# Revit family: BVN_BDKF
name_source: partatom
category: Mechanical Equipment
units: mm (PartAtom-declared; Revit-internal decimal feet)

## family parameters
Always vertical = Yes
Cut with Voids When Loaded = No
OmniClass Number = 23.75.00.00
OmniClass Title = Climate Control (HVAC)
Part Type = Breaks Into
Room Calculation Point = No
Round Connector Dimension = Use Diameter
Shared = No
Work Plane-Based = No

## types (13) — shared parameters
Description = Duct Fan
Frequency = 50 Hz
Manufacturer = Bahçıvan Elektrik Motor San. ve Tic. Ltd. Şti.
Material = <By Category>
Model = BDKF
Protection Class = 44
Sac = -2 mm  [stored -0.00656168 ft]
URL = http://www.bahcivanmotor.com.tr

## per-type parameters (varying)
| type | A | Air Flow | B | C | Capacitor | Corners | Current | D | E | F | G | Insulation Class | Power | Sound Pressure Level dB(A) | Speed ( d/d ) | Voltage | Weight |
| BDKF 30-15 | 150 mm | 450.0 m³/h | 300 mm | 400 mm  [stored 1.31234 ft] | 2.5 | 15 mm  [stored 0.0492126 ft] | 0 A | 320 mm  [stored 1.04987 ft] | 170 mm  [stored 0.557743 ft] | 350 mm  [stored 1.14829 ft] | 200 mm  [stored 0.656168 ft] | B | 95 W | 43 | 2450 | 230 V | 7.00 kg |
| BDKF 40-20A | 200 mm  [stored 0.656168 ft] | 1030.0 m³/h | 400 mm  [stored 1.31234 ft] | 500 mm  [stored 1.64042 ft] | 4 | 15 mm  [stored 0.0492126 ft] | 1 A | 420 mm  [stored 1.37795 ft] | 220 mm  [stored 0.721785 ft] | 450 mm  [stored 1.47638 ft] | 250 mm  [stored 0.82021 ft] | B | 135 W | 48 | 2870 | 230 V | 10.50 kg |
| BDKF 40-20B | 200 mm  [stored 0.656168 ft] | 1150.0 m³/h | 400 mm  [stored 1.31234 ft] | 500 mm  [stored 1.64042 ft] | 5 | 15 mm  [stored 0.0492126 ft] | 1 A | 420 mm  [stored 1.37795 ft] | 220 mm  [stored 0.721785 ft] | 450 mm  [stored 1.47638 ft] | 250 mm  [stored 0.82021 ft] | B | 180 W | 54 | 2650 | 230 V | 11.00 kg |
| BDKF 50-25 | 250 mm  [stored 0.82021 ft] | 1700.0 m³/h | 500 mm  [stored 1.64042 ft] | 565 mm  [stored 1.85367 ft] | 6 | 20 mm  [stored 0.0656168 ft] | 1 A | 520 mm  [stored 1.70604 ft] | 270 mm  [stored 0.885827 ft] | 550 mm | 300 mm | B | 240 W | 58 | 2750 | 230 V | 15.00 kg |
| BDKF 60-30 | 300 mm | 2180.0 m³/h | 600 mm | 650 mm  [stored 2.13255 ft] | 3 | 20 mm  [stored 0.0656168 ft] | 1 A | 620 mm  [stored 2.03412 ft] | 320 mm  [stored 1.04987 ft] | 650 mm  [stored 2.13255 ft] | 350 mm  [stored 1.14829 ft] | F | 155 W | 50 | 1650 | 230 V | 29.00 kg |
| BDKF 60-35A | 350 mm  [stored 1.14829 ft] | 2895.0 m³/h | 600 mm | 760 mm  [stored 2.49344 ft] | 3 | 20 mm  [stored 0.0656168 ft] | 1 A | 620 mm  [stored 2.03412 ft] | 370 mm  [stored 1.21391 ft] | 650 mm  [stored 2.13255 ft] | 400 mm  [stored 1.31234 ft] | F | 155 W | 53 | 1650 | 230 V | 31.00 kg |
| BDKF 60-35B | 350 mm  [stored 1.14829 ft] | 3900.0 m³/h | 600 mm | 760 mm  [stored 2.49344 ft] | 8 | 20 mm  [stored 0.0656168 ft] | 1 A | 620 mm  [stored 2.03412 ft] | 370 mm  [stored 1.21391 ft] | 650 mm  [stored 2.13255 ft] | 400 mm  [stored 1.31234 ft] | F | 270 W | 58 | 1680 | 230 V | 32.00 kg |
| BDKF 70-40A | 400 mm  [stored 1.31234 ft] | 4600.0 m³/h | 700 mm  [stored 2.29659 ft] | 800 mm  [stored 2.62467 ft] | 10 | 20 mm  [stored 0.0656168 ft] | 2 A | 720 mm  [stored 2.3622 ft] | 420 mm  [stored 1.37795 ft] | 750 mm  [stored 2.46063 ft] | 450 mm  [stored 1.47638 ft] | F | 440 W | 56 | 1150 | 230 V | 44.00 kg |
| BDKF 70-40B | 400 mm  [stored 1.31234 ft] | 5800.0 m³/h | 700 mm  [stored 2.29659 ft] | 800 mm  [stored 2.62467 ft] | 10 | 20 mm  [stored 0.0656168 ft] | 4 A | 720 mm  [stored 2.3622 ft] | 420 mm  [stored 1.37795 ft] | 750 mm  [stored 2.46063 ft] | 450 mm  [stored 1.47638 ft] | F | 775 W | 58 | 1450 | 230 V | 46.00 kg |
| BDKF 80-50 | 500 mm  [stored 1.64042 ft] | 7550.0 m³/h | 800 mm  [stored 2.62467 ft] | 920 mm  [stored 3.01837 ft] | 0 | 20 mm  [stored 0.0656168 ft] | 2 A | 820 mm  [stored 2.69029 ft] | 520 mm  [stored 1.70604 ft] | 850 mm  [stored 2.78871 ft] | 560 mm  [stored 1.83727 ft] | F | 960 W | 64 | 1335 | 380 V | 66.00 kg |
| BDKF 100-50 | 500 mm  [stored 1.64042 ft] | 9600.0 m³/h | 1000 mm  [stored 3.28084 ft] | 1050 mm | 0 | 20 mm  [stored 0.0656168 ft] | 3 A | 1030 mm  [stored 3.37927 ft] | 530 mm  [stored 1.73885 ft] | 1060 mm  [stored 3.47769 ft] | 560 mm  [stored 1.83727 ft] | F | 1400 W | 66 | 1250 | 380 V | 84.00 kg |
| BDKF 80-50M | 500 mm  [stored 1.64042 ft] | 6440.0 m³/h | 800 mm  [stored 2.62467 ft] | 920 mm  [stored 3.01837 ft] | 16 | 20 mm  [stored 0.0656168 ft] | 5 A | 820 mm  [stored 2.69029 ft] | 520 mm  [stored 1.70604 ft] | 850 mm  [stored 2.78871 ft] | 560 mm  [stored 1.83727 ft] | F | 1160 W | 64 | 1150 | 230 V | 72.00 kg |
| BDKF 100-50M | 500 mm  [stored 1.64042 ft] | 9600.0 m³/h | 1000 mm  [stored 3.28084 ft] | 1050 mm | 25 | 20 mm  [stored 0.0656168 ft] | 7 A | 1030 mm  [stored 3.37927 ft] | 530 mm  [stored 1.73885 ft] | 1060 mm  [stored 3.47769 ft] | 560 mm  [stored 1.83727 ft] | F | 1550 W | 66 | 1250 | 230 V | 84.00 kg |

note: [stored X ft] marks values corroborated as IEEE doubles in the binary element streams (Revit-internal decimal feet)

## geometry (parser evidence)
native form markers: Sweep x2
no freeform markers — native parametric forms only
